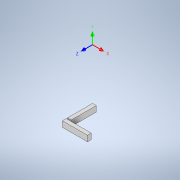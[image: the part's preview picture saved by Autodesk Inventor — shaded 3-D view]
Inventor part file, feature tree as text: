
AUTODESK INVENTOR PART (.ipt)
format: ipt  version: 2021 (Build 250183000, 183)  size: 121,856 bytes
history: native  units: mm
features: other x10, extrude x2, sketch x2
ambient origin geometry x8: Origin, YZ Plane, XZ Plane, XY Plane, X Axis, Y Axis, Z Axis, Center Point
bodies: Body1 (feature_tree)
feature tree (14):
  other  "Sólido1"
  extrude  "Extrusión1"  Depth=12000.0mm
  other  "SCU1"
  extrude  "Extrusión2"  Depth=80000.0mm
  sketch  "Boceto1"  dims[d0=80000.0mm d1=12000.0mm]
  sketch  "Boceto2"  dims[d2=12000.0mm d3=80000.0mm d5=18000.0mm d6=0.0mm d7=0.0mm d8=0.0mm d9=0.0mm d10=0.0mm d11=0.0mm d12=0.0mm d13=180000.0mm d14=288000.0mm d15=548000.0mm d17=4000.0mm d19=180000.0mm d20=180000.0mm d21=456000.0mm d22=1000.0mm d23=0.0mm d24=548000.0mm d25=456000.0mm]
  other  "Sólido2"
  other  "SCU1: Plano YZ"
  other  "SCU1: Plano XZ"
  other  "SCU1: Plano XY"
  other  "SCU1: Eje X"
  other  "SCU1: Eje Y"
  other  "SCU1: Eje Z"
  other  "SCU1: Centro"
